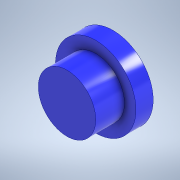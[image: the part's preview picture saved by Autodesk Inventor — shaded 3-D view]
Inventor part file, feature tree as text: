
AUTODESK INVENTOR PART (.ipt)
format: ipt  version: 2020 (Build 240168000, 168)  size: 111,104 bytes
history: native  units: mm
features: extrude x2, sketch x2
ambient origin geometry x8: Origin, YZ Plane, XZ Plane, XY Plane, X Axis, Y Axis, Z Axis, Center Point
bodies: Solid1 (feature_tree)
feature tree (4):
  extrude  "Extrusion1"  Depth=3.0mm TaperAngle=0.0deg
  extrude  "Extrusion2"  Depth=5.0mm TaperAngle=0.0deg
  sketch  "Sketch1"  dims[d0=14.0mm d1=3.0mm d2=0.0mm]
  sketch  "Sketch2"  dims[d3=10.0mm d4=5.0mm d5=0.0mm]
